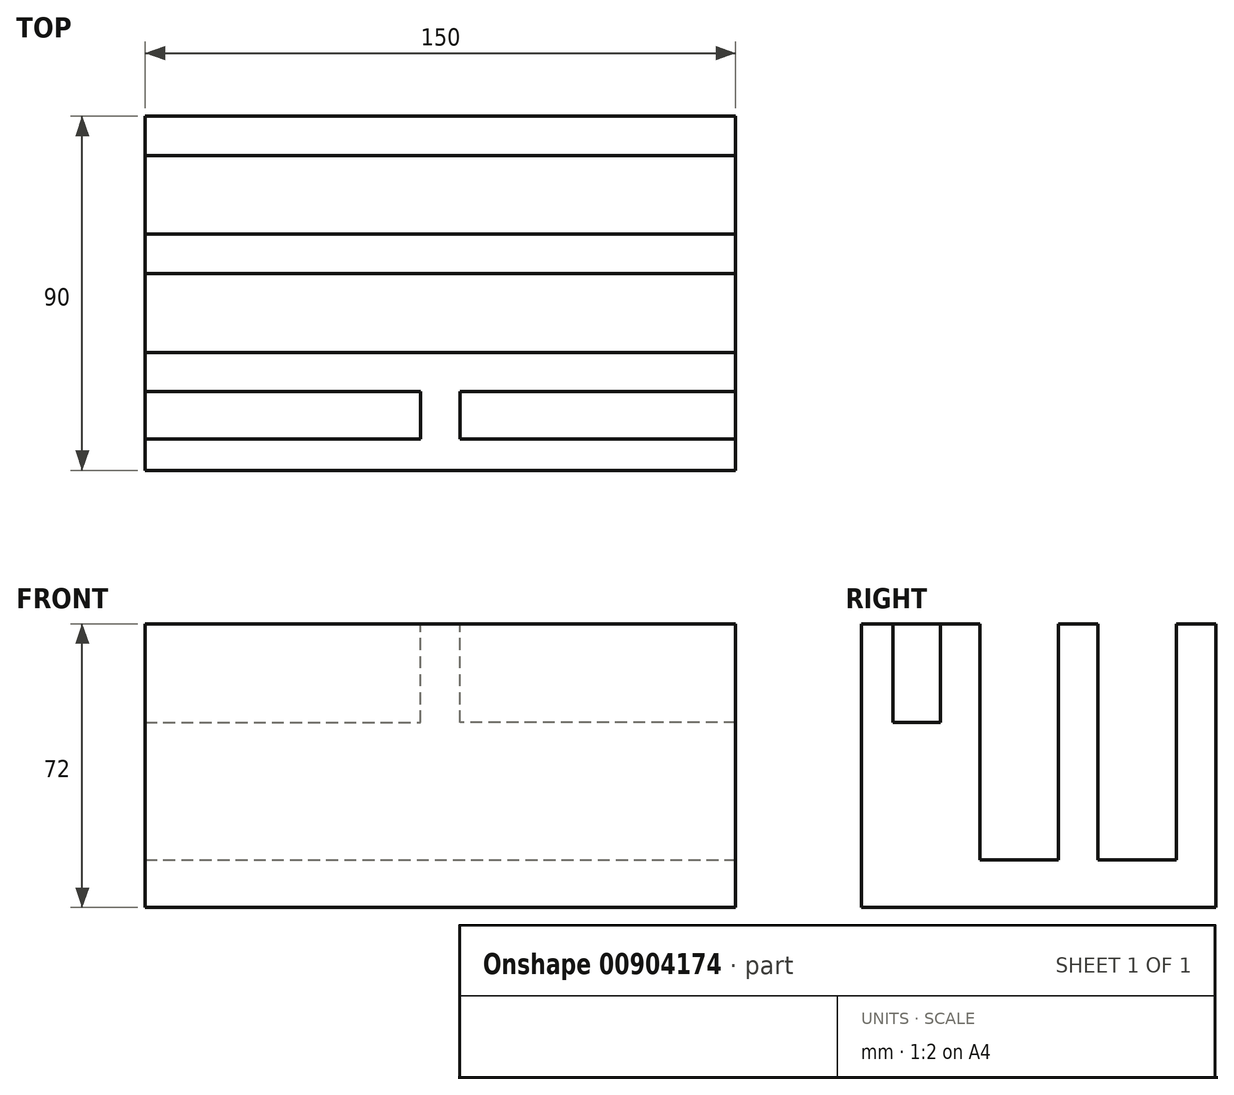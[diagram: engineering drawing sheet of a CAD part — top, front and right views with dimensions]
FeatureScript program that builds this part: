
annotation { "Feature Type Name" : "Feature", "Feature Type Description" : "" }
export const myFeature = defineFeature(function(context is Context, id is Id, definition is map)
    precondition{}
    {
        {
            var Q0;
            Q0=qCreatedBy(makeId("Top.planeOp"),FACE);
            var sketch = newSketch(context, id + "F0", { "sketchPlane" : qUnion([Q0])});
            skLineSegment(sketch, "E0.bottom", {"start": v(75, -45) * mm, "end": v(-75, -45) * mm});
            skLineSegment(sketch, "E0.top", {"start": v(75, 45) * mm, "end": v(-75, 45) * mm});
            skLineSegment(sketch, "E0.left", {"start": v(75, -45) * mm, "end": v(75, 45) * mm});
            skLineSegment(sketch, "E0.right", {"start": v(-75, -45) * mm, "end": v(-75, 45) * mm});
            skPoint(sketch, "E0.middle", {"position": v(0, 0) * mm});
            skSolve(sketch);
        }
        {
            var Q0;
            Q0=makeQuery(id+"F0.imprint","IMPRINT",FACE,{"disambiguationData":[TD([[makeQuery(id+"F0.imprint","IMPRINT",EDGE,{"derivedFrom":sQuery(id+"F0.wireOp",EDGE,"E0.bottom")}),-1.0]])]});
            extrude(context, id + "F1", {"entities" : qUnion([Q0]), "depth" : 72 * mm, "offsetDistance" : 25 * mm});
        }
        {
            var Q0;
            Q0=makeQuery(id+"F1.opExtrude","CAP_FACE",FACE,{"disambiguationData":[OSD([sQuery(id+"F0.wireOp",EDGE,"E0.bottom"),sQuery(id+"F0.wireOp",EDGE,"E0.top"),sQuery(id+"F0.wireOp",EDGE,"E0.left"),sQuery(id+"F0.wireOp",EDGE,"E0.right")])],"isStart":false});
            var sketch = newSketch(context, id + "F2", { "sketchPlane" : qUnion([Q0])});
            skLineSegment(sketch, "E1.bottom", {"start": v(-75, -25) * mm, "end": v(-5, -25) * mm});
            skLineSegment(sketch, "E1.top", {"start": v(-75, -37) * mm, "end": v(-5, -37) * mm});
            skLineSegment(sketch, "E1.left", {"start": v(-75, -25) * mm, "end": v(-75, -37) * mm});
            skLineSegment(sketch, "E1.right", {"start": v(-5, -25) * mm, "end": v(-5, -37) * mm});
            skLineSegment(sketch, "E2.bottom", {"start": v(75, -25) * mm, "end": v(5, -25) * mm});
            skLineSegment(sketch, "E2.top", {"start": v(75, -37) * mm, "end": v(5, -37) * mm});
            skLineSegment(sketch, "E2.left", {"start": v(75, -25) * mm, "end": v(75, -37) * mm});
            skLineSegment(sketch, "E2.right", {"start": v(5, -25) * mm, "end": v(5, -37) * mm});
            skSolve(sketch);
        }
        {
            var Q0;
            Q0=makeQuery(id+"F2.imprint","IMPRINT",FACE,{"disambiguationData":[TD([[makeQuery(id+"F2.imprint","IMPRINT",EDGE,{"derivedFrom":sQuery(id+"F2.wireOp",EDGE,"E1.bottom")}),-1.0]])]});
            var Q1;
            Q1=makeQuery(id+"F2.imprint","IMPRINT",FACE,{"disambiguationData":[TD([[makeQuery(id+"F2.imprint","IMPRINT",EDGE,{"derivedFrom":sQuery(id+"F2.wireOp",EDGE,"E2.bottom")}),1.0]])]});
            extrude(context, id + "F3", {"entities" : qUnion([Q0, Q1]), "operationType" : NewBodyOperationType.REMOVE, "oppositeDirection" : true, "depth" : 25 * mm, "offsetDistance" : 25 * mm});
        }
        {
            var Q0;
            Q0=makeQuery(id+"F1.opExtrude","CAP_FACE",FACE,{"disambiguationData":[OSD([sQuery(id+"F0.wireOp",EDGE,"E0.bottom"),sQuery(id+"F0.wireOp",EDGE,"E0.top"),sQuery(id+"F0.wireOp",EDGE,"E0.left"),sQuery(id+"F0.wireOp",EDGE,"E0.right")])],"isStart":false});
            var sketch = newSketch(context, id + "F4", { "sketchPlane" : qUnion([Q0])});
            skLineSegment(sketch, "E3.bottom", {"start": v(-75, 35) * mm, "end": v(75, 35) * mm});
            skLineSegment(sketch, "E3.top", {"start": v(-75, 15) * mm, "end": v(75, 15) * mm});
            skLineSegment(sketch, "E3.left", {"start": v(-75, 35) * mm, "end": v(-75, 15) * mm});
            skLineSegment(sketch, "E3.right", {"start": v(75, 35) * mm, "end": v(75, 15) * mm});
            skLineSegment(sketch, "E4.bottom", {"start": v(-75, 5) * mm, "end": v(75, 5) * mm});
            skLineSegment(sketch, "E4.top", {"start": v(-75, -15) * mm, "end": v(75, -15) * mm});
            skLineSegment(sketch, "E4.left", {"start": v(-75, 5) * mm, "end": v(-75, -15) * mm});
            skLineSegment(sketch, "E4.right", {"start": v(75, 5) * mm, "end": v(75, -15) * mm});
            skSolve(sketch);
        }
        {
            var Q0;
            Q0=makeQuery(id+"F4.imprint","IMPRINT",FACE,{"disambiguationData":[TD([[makeQuery(id+"F4.imprint","IMPRINT",EDGE,{"derivedFrom":sQuery(id+"F4.wireOp",EDGE,"E3.bottom")}),-1.0]])]});
            var Q1;
            Q1=makeQuery(id+"F4.imprint","IMPRINT",FACE,{"disambiguationData":[TD([[makeQuery(id+"F4.imprint","IMPRINT",EDGE,{"derivedFrom":sQuery(id+"F4.wireOp",EDGE,"E4.bottom")}),-1.0]])]});
            extrude(context, id + "F5", {"entities" : qUnion([Q0, Q1]), "operationType" : NewBodyOperationType.REMOVE, "oppositeDirection" : true, "depth" : 60 * mm, "offsetDistance" : 25 * mm});
        }
    });
